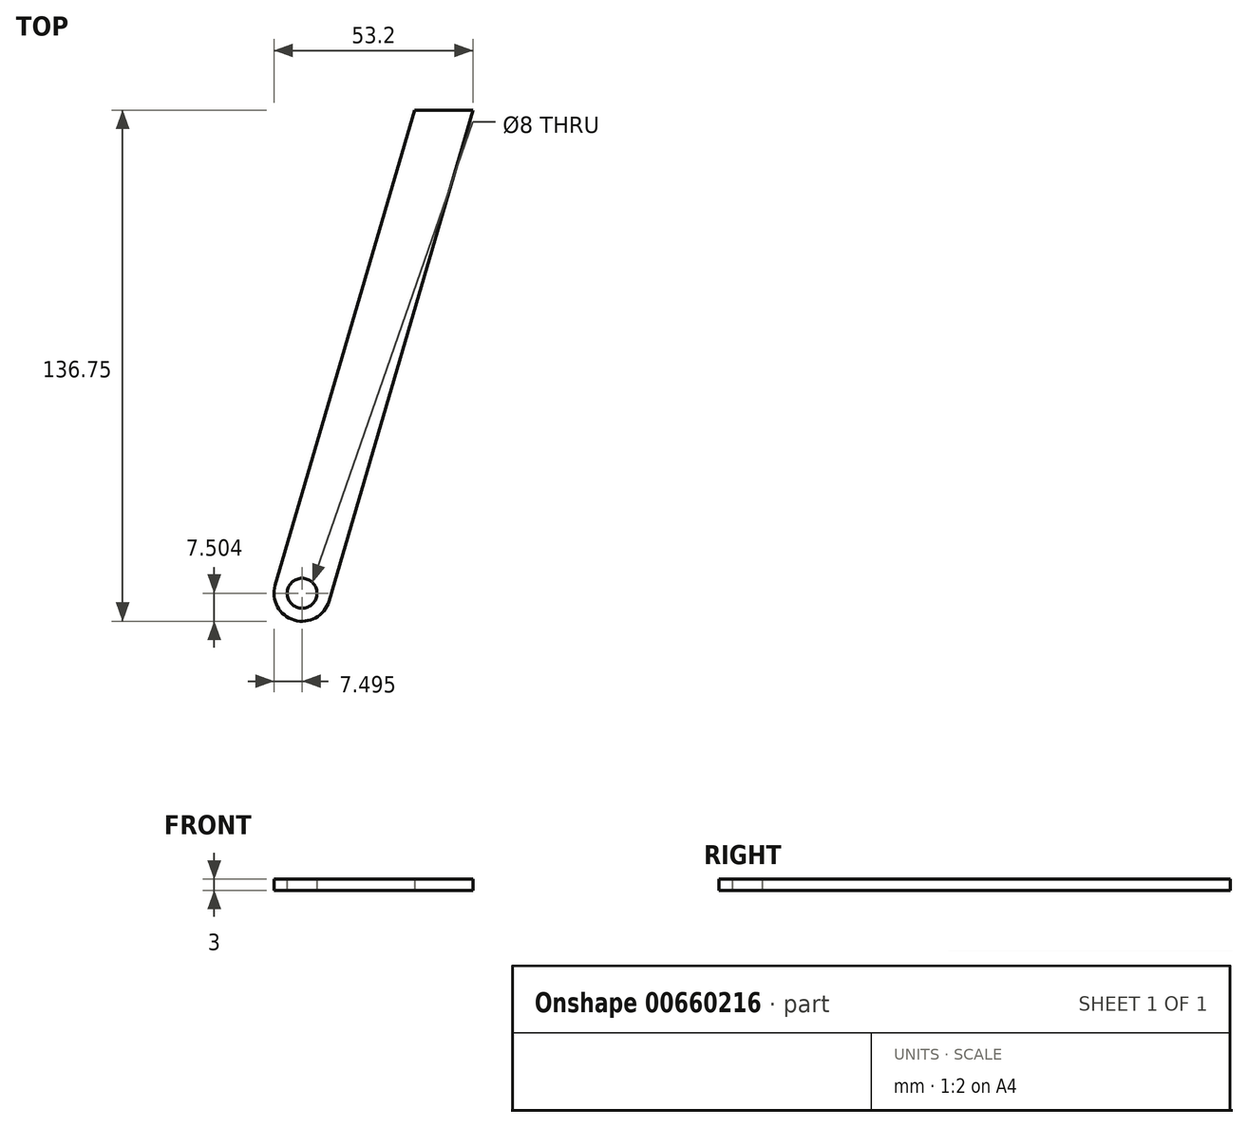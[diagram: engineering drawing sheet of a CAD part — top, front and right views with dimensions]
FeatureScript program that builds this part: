
annotation { "Feature Type Name" : "Feature", "Feature Type Description" : "" }
export const myFeature = defineFeature(function(context is Context, id is Id, definition is map)
    precondition{}
    {
        {
            var Q0;
            Q0=qCreatedBy(makeId("Top.planeOp"),FACE);
            var sketch = newSketch(context, id + "F0", { "sketchPlane" : qUnion([Q0])});
            skLineSegment(sketch, "E0", {"start": v(0, 0) * mm, "end": v(-42.2, -143.94) * mm, "construction": true});
            skLineSegment(sketch, "E1", {"start": v(-42.2, -143.94) * mm, "end": v(-42.2, -143.94) * mm});
            skLineSegment(sketch, "E2", {"start": v(-47.28, -134.64) * mm, "end": v(-11.48, -12.5) * mm});
            skLineSegment(sketch, "E3", {"start": v(-32.89, -138.86) * mm, "end": v(4.04, -12.9) * mm});
            skPoint(sketch, "E4.orphan", {"position": v(-56.59, -139.72) * mm});
            skCircle(sketch, "E5", {"center": v(-40.08, -136.75) * mm, "radius": 4 * mm});
            skPoint(sketch, "E6.visualSharp", {"position": v(-49.4, -141.83) * mm});
            skArc(sketch, "E6.filletArc", {"start": v(-47.28, -134.64) * mm, "mid": v(-46.67, -140.34) * mm, "end": v(-42.2, -143.94) * mm});
            skPoint(sketch, "E7.visualSharp", {"position": v(-35, -146.05) * mm});
            skArc(sketch, "E7.filletArc", {"start": v(-42.2, -143.94) * mm, "mid": v(-36.49, -143.33) * mm, "end": v(-32.89, -138.86) * mm});
            skLineSegment(sketch, "E8", {"start": v(-11.48, -12.5) * mm, "end": v(-10.01, -7.5) * mm});
            skLineSegment(sketch, "E9", {"start": v(-10.01, -7.5) * mm, "end": v(5.62, -7.5) * mm});
            skLineSegment(sketch, "E10", {"start": v(4.04, -12.9) * mm, "end": v(5.62, -7.5) * mm});
            skSolve(sketch);
        }
        {
            var Q0;
            Q0=makeQuery(id+"F0.imprint","IMPRINT",FACE,{"disambiguationData":[TD([[makeQuery(id+"F0.imprint","IMPRINT",EDGE,{"derivedFrom":sQuery(id+"F0.wireOp",EDGE,"xLPQFgd9-T2cH-qlGg-8KEg-PCly6ktcjAdA.bottom")}),-1.0]])]});
            var Q1;
            Q1=makeQuery(id+"F0.imprint","IMPRINT",FACE,{"disambiguationData":[TD([[makeQuery(id+"F0.imprint","IMPRINT",EDGE,{"derivedFrom":sQuery(id+"F0.wireOp",EDGE,"E2")}),-1.0]])]});
            extrude(context, id + "F1", {"entities" : qUnion([Q0, Q1]), "depth" : 3 * mm, "offsetDistance" : 25 * mm});
        }
    });
